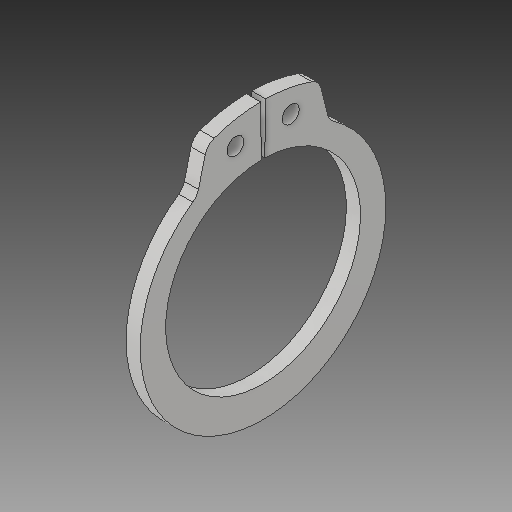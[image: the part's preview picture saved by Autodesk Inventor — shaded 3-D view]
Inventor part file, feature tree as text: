
AUTODESK INVENTOR PART (.ipt)
format: ipt  version: 2017 (Build 210142000, 142)  size: 112,128 bytes
history: native  units: in
note: dims shown in document units (in); Inventor stores cm internally (conversion verified against a paired STEP export)
features: fillet x1
ambient origin geometry x8: Origin, YZ Plane, XZ Plane, XY Plane, X Axis, Y Axis, Z Axis, Center Point
bodies: Solid1 (feature_tree)
feature tree (1):
  fillet  "Fillet1"  [1 undecoded]
note: 1 required parameter value undecoded (feature->parameter linkage not recoverable at this tier; creation-order binding heuristic only, values carry confidence <= 0.55)
